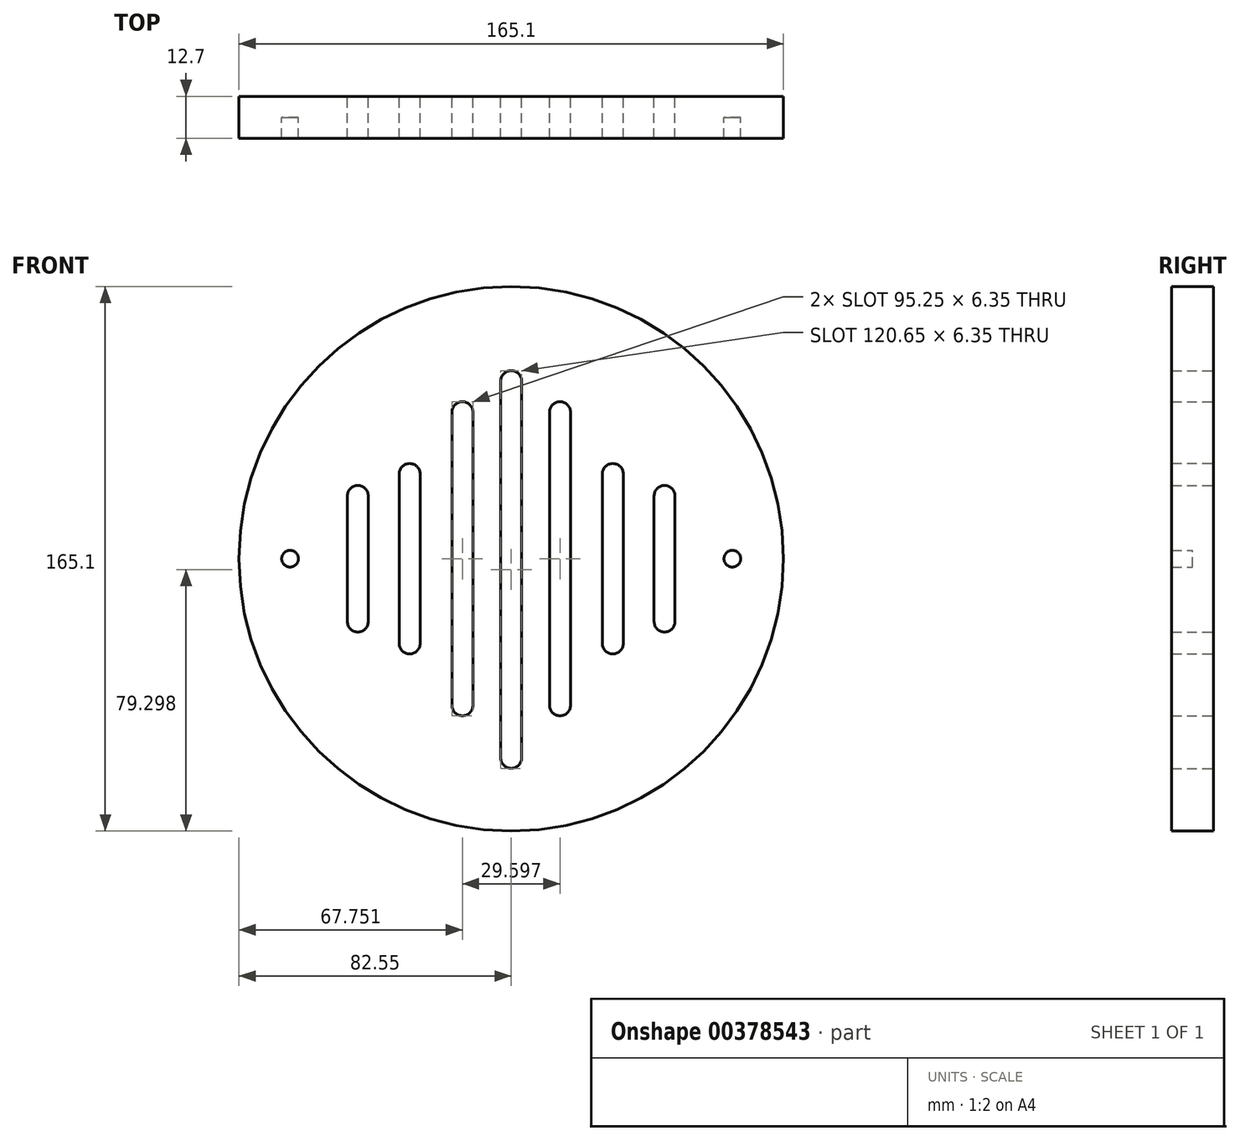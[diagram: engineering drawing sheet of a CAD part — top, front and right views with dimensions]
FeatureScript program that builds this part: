
annotation { "Feature Type Name" : "Feature", "Feature Type Description" : "" }
export const myFeature = defineFeature(function(context is Context, id is Id, definition is map)
    precondition{}
    {
        {
            var Q0;
            Q0=qCreatedBy(makeId("Front.planeOp"),FACE);
            var sketch = newSketch(context, id + "F0", { "sketchPlane" : qUnion([Q0])});
            skCircle(sketch, "E0", {"center": v(0, 0) * mm, "radius": 82.55 * mm});
            skLineSegment(sketch, "E1.bottom", {"start": v(0, -63.58) * mm, "end": v(0, -63.58) * mm});
            skLineSegment(sketch, "E1.top", {"start": v(0, 57.07) * mm, "end": v(0, 57.07) * mm});
            skLineSegment(sketch, "E1.left", {"start": v(3.18, -60.4) * mm, "end": v(3.18, 53.9) * mm});
            skLineSegment(sketch, "E1.right", {"start": v(-3.17, -60.4) * mm, "end": v(-3.17, 53.9) * mm});
            skPoint(sketch, "E2.visualSharp", {"position": v(-3.17, 57.07) * mm});
            skArc(sketch, "E2.filletArc", {"start": v(0, 57.07) * mm, "mid": v(-2.25, 56.14) * mm, "end": v(-3.17, 53.9) * mm});
            skPoint(sketch, "E3.visualSharp", {"position": v(3.18, 57.07) * mm});
            skArc(sketch, "E3.filletArc", {"start": v(3.18, 53.9) * mm, "mid": v(2.25, 56.14) * mm, "end": v(0, 57.07) * mm});
            skPoint(sketch, "E4.visualSharp", {"position": v(-3.17, -63.58) * mm});
            skArc(sketch, "E4.filletArc", {"start": v(-3.17, -60.4) * mm, "mid": v(-2.25, -62.65) * mm, "end": v(0, -63.58) * mm});
            skPoint(sketch, "E5.visualSharp", {"position": v(3.18, -63.58) * mm});
            skArc(sketch, "E5.filletArc", {"start": v(0, -63.58) * mm, "mid": v(2.25, -62.65) * mm, "end": v(3.18, -60.4) * mm});
            skLineSegment(sketch, "E6.bottom", {"start": v(-14.8, 47.63) * mm, "end": v(-14.8, 47.63) * mm});
            skLineSegment(sketch, "E6.top", {"start": v(-14.8, -47.63) * mm, "end": v(-14.8, -47.63) * mm});
            skLineSegment(sketch, "E6.left", {"start": v(-17.97, 44.45) * mm, "end": v(-17.97, -44.45) * mm});
            skLineSegment(sketch, "E6.right", {"start": v(-11.62, 44.45) * mm, "end": v(-11.62, -44.45) * mm});
            skPoint(sketch, "E6.middle", {"position": v(-14.8, 0) * mm});
            skLineSegment(sketch, "E7.bottom", {"start": v(-30.8, 28.9) * mm, "end": v(-30.8, 28.9) * mm});
            skLineSegment(sketch, "E7.top", {"start": v(-30.8, -28.9) * mm, "end": v(-30.8, -28.9) * mm});
            skLineSegment(sketch, "E7.left", {"start": v(-33.98, 25.72) * mm, "end": v(-33.98, -25.72) * mm});
            skLineSegment(sketch, "E7.right", {"start": v(-27.63, 25.72) * mm, "end": v(-27.63, -25.72) * mm});
            skPoint(sketch, "E7.middle", {"position": v(-30.8, 0) * mm});
            skLineSegment(sketch, "E8.bottom", {"start": v(-46.5, 22.23) * mm, "end": v(-46.5, 22.23) * mm});
            skLineSegment(sketch, "E8.top", {"start": v(-46.5, -22.23) * mm, "end": v(-46.5, -22.23) * mm});
            skLineSegment(sketch, "E8.left", {"start": v(-49.68, 19.05) * mm, "end": v(-49.68, -19.05) * mm});
            skLineSegment(sketch, "E8.right", {"start": v(-43.33, 19.05) * mm, "end": v(-43.33, -19.05) * mm});
            skPoint(sketch, "E8.middle", {"position": v(-46.5, 0) * mm});
            skPoint(sketch, "E9.visualSharp", {"position": v(-49.68, 22.23) * mm});
            skArc(sketch, "E9.filletArc", {"start": v(-46.5, 22.23) * mm, "mid": v(-48.75, 21.3) * mm, "end": v(-49.68, 19.05) * mm});
            skPoint(sketch, "E10.visualSharp", {"position": v(-43.33, 22.23) * mm});
            skArc(sketch, "E10.filletArc", {"start": v(-43.33, 19.05) * mm, "mid": v(-44.26, 21.3) * mm, "end": v(-46.5, 22.23) * mm});
            skPoint(sketch, "E11.visualSharp", {"position": v(-49.68, -22.23) * mm});
            skArc(sketch, "E11.filletArc", {"start": v(-49.68, -19.05) * mm, "mid": v(-48.75, -21.3) * mm, "end": v(-46.5, -22.23) * mm});
            skPoint(sketch, "E12.visualSharp", {"position": v(-43.33, -22.23) * mm});
            skArc(sketch, "E12.filletArc", {"start": v(-46.5, -22.23) * mm, "mid": v(-44.26, -21.3) * mm, "end": v(-43.33, -19.05) * mm});
            skPoint(sketch, "E13.visualSharp", {"position": v(-33.98, -28.9) * mm});
            skArc(sketch, "E13.filletArc", {"start": v(-33.98, -25.72) * mm, "mid": v(-33.05, -27.96) * mm, "end": v(-30.8, -28.9) * mm});
            skPoint(sketch, "E14.visualSharp", {"position": v(-27.63, -28.9) * mm});
            skArc(sketch, "E14.filletArc", {"start": v(-30.8, -28.9) * mm, "mid": v(-28.56, -27.96) * mm, "end": v(-27.63, -25.72) * mm});
            skPoint(sketch, "E15.visualSharp", {"position": v(-33.98, 28.9) * mm});
            skArc(sketch, "E15.filletArc", {"start": v(-30.8, 28.9) * mm, "mid": v(-33.05, 27.96) * mm, "end": v(-33.98, 25.72) * mm});
            skPoint(sketch, "E16.visualSharp", {"position": v(-27.63, 28.9) * mm});
            skArc(sketch, "E16.filletArc", {"start": v(-27.63, 25.72) * mm, "mid": v(-28.56, 27.96) * mm, "end": v(-30.8, 28.9) * mm});
            skPoint(sketch, "E17.visualSharp", {"position": v(-11.62, 47.63) * mm});
            skArc(sketch, "E17.filletArc", {"start": v(-11.62, 44.45) * mm, "mid": v(-12.55, 46.7) * mm, "end": v(-14.8, 47.63) * mm});
            skPoint(sketch, "E18.visualSharp", {"position": v(-17.97, 47.63) * mm});
            skArc(sketch, "E18.filletArc", {"start": v(-14.8, 47.63) * mm, "mid": v(-17.04, 46.7) * mm, "end": v(-17.97, 44.45) * mm});
            skPoint(sketch, "E19.visualSharp", {"position": v(-11.62, -47.63) * mm});
            skArc(sketch, "E19.filletArc", {"start": v(-14.8, -47.63) * mm, "mid": v(-12.55, -46.7) * mm, "end": v(-11.62, -44.45) * mm});
            skPoint(sketch, "E20.visualSharp", {"position": v(-17.97, -47.63) * mm});
            skArc(sketch, "E20.filletArc", {"start": v(-17.97, -44.45) * mm, "mid": v(-17.04, -46.7) * mm, "end": v(-14.8, -47.63) * mm});
            skArc(sketch, "E21.MirrorCS", {"start": v(30.8, -28.9) * mm, "mid": v(28.56, -27.96) * mm, "end": v(27.63, -25.72) * mm});
            skArc(sketch, "E22.MirrorCS", {"start": v(30.8, 28.9) * mm, "mid": v(33.05, 27.96) * mm, "end": v(33.98, 25.72) * mm});
            skArc(sketch, "E23.MirrorCS", {"start": v(14.8, 47.63) * mm, "mid": v(17.04, 46.7) * mm, "end": v(17.97, 44.45) * mm});
            skArc(sketch, "E24.MirrorCS", {"start": v(46.5, 22.23) * mm, "mid": v(48.75, 21.3) * mm, "end": v(49.68, 19.05) * mm});
            skArc(sketch, "E25.MirrorCS", {"start": v(43.33, 19.05) * mm, "mid": v(44.26, 21.3) * mm, "end": v(46.5, 22.23) * mm});
            skArc(sketch, "E26.MirrorCS", {"start": v(49.68, -19.05) * mm, "mid": v(48.75, -21.3) * mm, "end": v(46.5, -22.23) * mm});
            skArc(sketch, "E27.MirrorCS", {"start": v(14.8, -47.63) * mm, "mid": v(12.55, -46.7) * mm, "end": v(11.62, -44.45) * mm});
            skArc(sketch, "E28.MirrorCS", {"start": v(46.5, -22.23) * mm, "mid": v(44.26, -21.3) * mm, "end": v(43.33, -19.05) * mm});
            skArc(sketch, "E29.MirrorCS", {"start": v(17.97, -44.45) * mm, "mid": v(17.04, -46.7) * mm, "end": v(14.8, -47.63) * mm});
            skLineSegment(sketch, "E30.MirrorCS", {"start": v(46.5, -22.23) * mm, "end": v(46.5, -22.23) * mm});
            skArc(sketch, "E31.MirrorCS", {"start": v(11.62, 44.45) * mm, "mid": v(12.55, 46.7) * mm, "end": v(14.8, 47.63) * mm});
            skArc(sketch, "E32.MirrorCS", {"start": v(33.98, -25.72) * mm, "mid": v(33.05, -27.96) * mm, "end": v(30.8, -28.9) * mm});
            skArc(sketch, "E33.MirrorCS", {"start": v(27.63, 25.72) * mm, "mid": v(28.56, 27.96) * mm, "end": v(30.8, 28.9) * mm});
            skPoint(sketch, "E34.MirrorP", {"position": v(14.8, 0) * mm});
            skLineSegment(sketch, "E35.MirrorCS", {"start": v(30.8, -28.9) * mm, "end": v(30.8, -28.9) * mm});
            skPoint(sketch, "E36.MirrorP", {"position": v(27.63, 28.9) * mm});
            skLineSegment(sketch, "E37.MirrorCS", {"start": v(46.5, 22.23) * mm, "end": v(46.5, 22.23) * mm});
            skPoint(sketch, "E38.MirrorP", {"position": v(17.97, -47.63) * mm});
            skPoint(sketch, "E39.MirrorP", {"position": v(30.8, 0) * mm});
            skPoint(sketch, "E40.MirrorP", {"position": v(43.33, -22.23) * mm});
            skLineSegment(sketch, "E41.MirrorCS", {"start": v(33.98, 25.72) * mm, "end": v(33.98, -25.72) * mm});
            skLineSegment(sketch, "E42.MirrorCS", {"start": v(11.62, 44.45) * mm, "end": v(11.62, -44.45) * mm});
            skLineSegment(sketch, "E43.MirrorCS", {"start": v(17.97, 44.45) * mm, "end": v(17.97, -44.45) * mm});
            skLineSegment(sketch, "E44.MirrorCS", {"start": v(27.63, 25.72) * mm, "end": v(27.63, -25.72) * mm});
            skLineSegment(sketch, "E45.MirrorCS", {"start": v(49.68, 19.05) * mm, "end": v(49.68, -19.05) * mm});
            skLineSegment(sketch, "E46.MirrorCS", {"start": v(14.8, 47.63) * mm, "end": v(14.8, 47.63) * mm});
            skPoint(sketch, "E47.MirrorP", {"position": v(49.68, -22.23) * mm});
            skPoint(sketch, "E48.MirrorP", {"position": v(46.5, 0) * mm});
            skPoint(sketch, "E49.MirrorP", {"position": v(17.97, 47.63) * mm});
            skPoint(sketch, "E50.MirrorP", {"position": v(11.62, -47.63) * mm});
            skLineSegment(sketch, "E51.MirrorCS", {"start": v(43.33, 19.05) * mm, "end": v(43.33, -19.05) * mm});
            skPoint(sketch, "E52.MirrorP", {"position": v(49.68, 22.23) * mm});
            skPoint(sketch, "E53.MirrorP", {"position": v(33.98, 28.9) * mm});
            skLineSegment(sketch, "E54.MirrorCS", {"start": v(30.8, 28.9) * mm, "end": v(30.8, 28.9) * mm});
            skLineSegment(sketch, "E55.MirrorCS", {"start": v(14.8, -47.63) * mm, "end": v(14.8, -47.63) * mm});
            skPoint(sketch, "E56.MirrorP", {"position": v(11.62, 47.63) * mm});
            skPoint(sketch, "E57.MirrorP", {"position": v(33.98, -28.9) * mm});
            skPoint(sketch, "E58.MirrorP", {"position": v(43.33, 22.23) * mm});
            skPoint(sketch, "E59.MirrorP", {"position": v(27.63, -28.9) * mm});
            skSolve(sketch);
        }
        {
            var Q0;
            Q0=makeQuery(id+"F0.imprint","IMPRINT",FACE,{"disambiguationData":[TD([[makeQuery(id+"F0.imprint","IMPRINT",EDGE,{"derivedFrom":sQuery(id+"F0.wireOp",EDGE,"E0")}),1.0]])]});
            extrude(context, id + "F1", {"entities" : qUnion([Q0]), "depth" : 6.35 * mm});
        }
        {
            var Q0;
            Q0=makeQuery(id+"F1.opExtrude","CAP_FACE",FACE,{"disambiguationData":[OSD([sQuery(id+"F0.wireOp",EDGE,"E0"),sQuery(id+"F0.wireOp",EDGE,"E1.left"),sQuery(id+"F0.wireOp",EDGE,"E1.right"),sQuery(id+"F0.wireOp",EDGE,"E2.filletArc"),sQuery(id+"F0.wireOp",EDGE,"E3.filletArc"),sQuery(id+"F0.wireOp",EDGE,"E4.filletArc"),sQuery(id+"F0.wireOp",EDGE,"E5.filletArc"),sQuery(id+"F0.wireOp",EDGE,"E6.left"),sQuery(id+"F0.wireOp",EDGE,"E6.right"),sQuery(id+"F0.wireOp",EDGE,"E7.left"),sQuery(id+"F0.wireOp",EDGE,"E7.right"),sQuery(id+"F0.wireOp",EDGE,"E8.left"),sQuery(id+"F0.wireOp",EDGE,"E8.right"),sQuery(id+"F0.wireOp",EDGE,"E9.filletArc"),sQuery(id+"F0.wireOp",EDGE,"E10.filletArc"),sQuery(id+"F0.wireOp",EDGE,"E11.filletArc"),sQuery(id+"F0.wireOp",EDGE,"E12.filletArc"),sQuery(id+"F0.wireOp",EDGE,"E13.filletArc"),sQuery(id+"F0.wireOp",EDGE,"E14.filletArc"),sQuery(id+"F0.wireOp",EDGE,"E15.filletArc"),sQuery(id+"F0.wireOp",EDGE,"E16.filletArc"),sQuery(id+"F0.wireOp",EDGE,"E17.filletArc"),sQuery(id+"F0.wireOp",EDGE,"E18.filletArc"),sQuery(id+"F0.wireOp",EDGE,"E19.filletArc"),sQuery(id+"F0.wireOp",EDGE,"E20.filletArc"),sQuery(id+"F0.wireOp",EDGE,"E21.MirrorCS"),sQuery(id+"F0.wireOp",EDGE,"E22.MirrorCS"),sQuery(id+"F0.wireOp",EDGE,"E23.MirrorCS"),sQuery(id+"F0.wireOp",EDGE,"E24.MirrorCS"),sQuery(id+"F0.wireOp",EDGE,"E25.MirrorCS"),sQuery(id+"F0.wireOp",EDGE,"E26.MirrorCS"),sQuery(id+"F0.wireOp",EDGE,"E27.MirrorCS"),sQuery(id+"F0.wireOp",EDGE,"E28.MirrorCS"),sQuery(id+"F0.wireOp",EDGE,"E29.MirrorCS"),sQuery(id+"F0.wireOp",EDGE,"E31.MirrorCS"),sQuery(id+"F0.wireOp",EDGE,"E32.MirrorCS"),sQuery(id+"F0.wireOp",EDGE,"E33.MirrorCS"),sQuery(id+"F0.wireOp",EDGE,"E41.MirrorCS"),sQuery(id+"F0.wireOp",EDGE,"E42.MirrorCS"),sQuery(id+"F0.wireOp",EDGE,"E43.MirrorCS"),sQuery(id+"F0.wireOp",EDGE,"E44.MirrorCS"),sQuery(id+"F0.wireOp",EDGE,"E45.MirrorCS"),sQuery(id+"F0.wireOp",EDGE,"E51.MirrorCS")])],"isStart":false});
            var sketch = newSketch(context, id + "F2", { "sketchPlane" : qUnion([Q0])});
            skCircle(sketch, "E60", {"center": v(-67.05, 0) * mm, "radius": 2.54 * mm});
            skCircle(sketch, "E61.MirrorC", {"center": v(67.05, 0) * mm, "radius": 2.54 * mm});
            skSolve(sketch);
        }
        {
            var Q0;
            Q0=makeQuery(id+"F2.imprint","IMPRINT",FACE,{"disambiguationData":[TD([[makeQuery(id+"F2.imprint","IMPRINT",EDGE,{"derivedFrom":sQuery(id+"F2.wireOp",EDGE,"E60")}),-1.0]])]});
            extrude(context, id + "F3", {"entities" : qUnion([Q0]), "operationType" : NewBodyOperationType.ADD, "depth" : 6.35 * mm});
        }
    });
